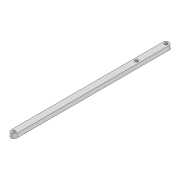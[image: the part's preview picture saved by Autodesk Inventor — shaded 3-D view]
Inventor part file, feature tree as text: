
AUTODESK INVENTOR PART (.ipt)
format: ipt  version: 2022 (Build 260153000, 153)  size: 89,600 bytes
history: native  units: mm
features: extrude x1, sketch x1
ambient origin geometry x8: Origin, YZ Plane, XZ Plane, XY Plane, X Axis, Y Axis, Z Axis, Center Point
bodies: Solid1 (feature_tree)
feature tree (2):
  extrude  "Extrusion1"  Depth=120.253mm
  sketch  "Sketch1"  dims[d0=3.2mm d1=3.2mm d2=6.0mm d3=149.329mm d6=4.0mm d7=0.0mm d14=3.2mm d15=120.253mm]
